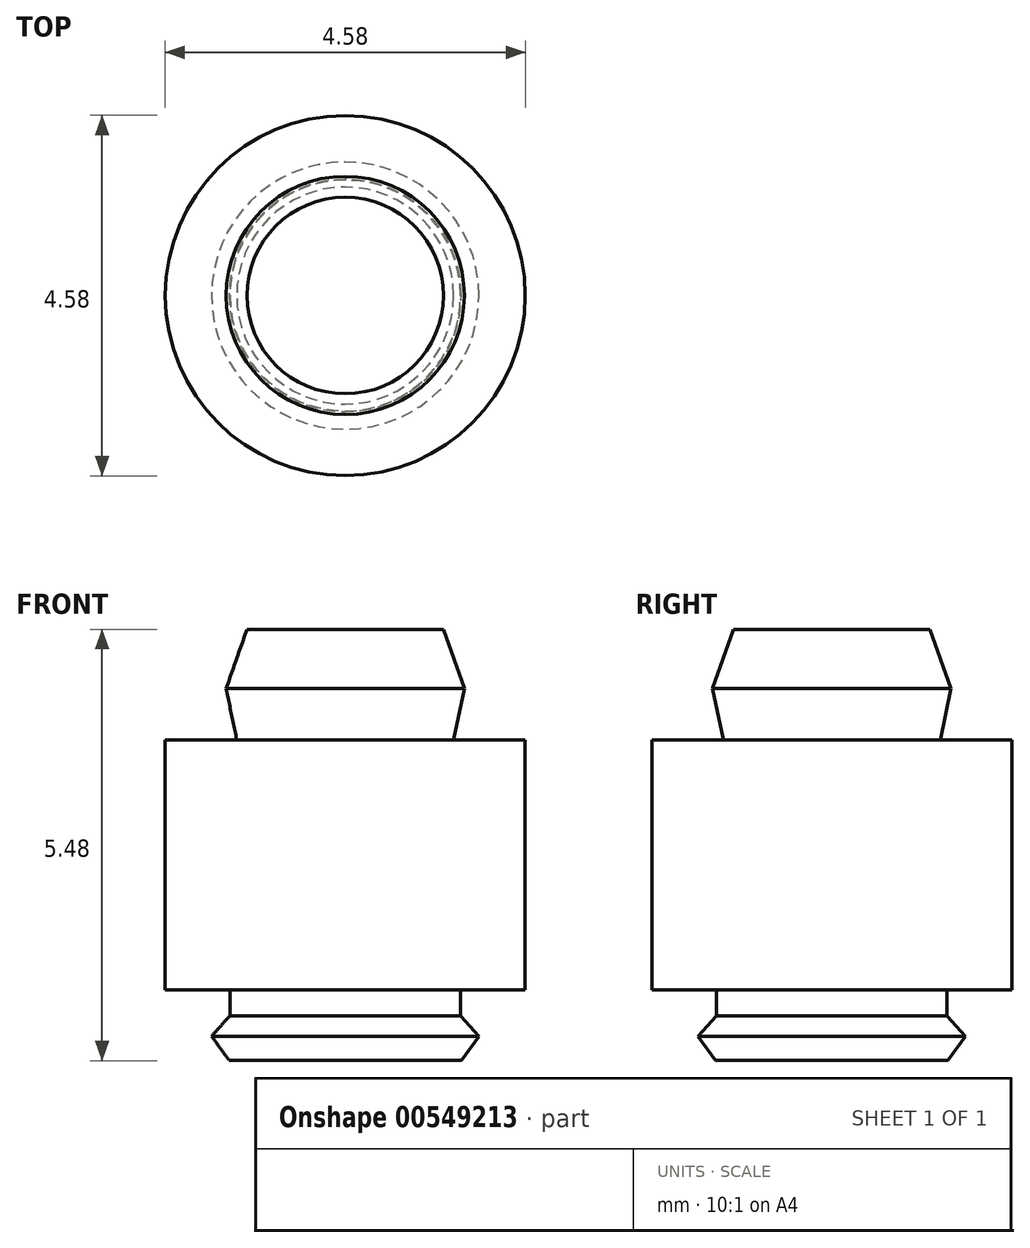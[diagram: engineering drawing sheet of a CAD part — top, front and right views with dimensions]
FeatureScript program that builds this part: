
annotation { "Feature Type Name" : "Feature", "Feature Type Description" : "" }
export const myFeature = defineFeature(function(context is Context, id is Id, definition is map)
    precondition{}
    {
        {
            var Q0;
            Q0=qCreatedBy(makeId("Front.planeOp"),FACE);
            var sketch = newSketch(context, id + "F0", { "sketchPlane" : qUnion([Q0])});
            skLineSegment(sketch, "E0", {"start": v(0, 0) * mm, "end": v(0, 4.84) * mm});
            skLineSegment(sketch, "E1", {"start": v(0, 3.18) * mm, "end": v(2.29, 3.18) * mm});
            skLineSegment(sketch, "E2", {"start": v(2.29, 3.18) * mm, "end": v(2.29, 0) * mm});
            skLineSegment(sketch, "E3", {"start": v(2.29, 0) * mm, "end": v(0, 0) * mm});
            skLineSegment(sketch, "E4", {"start": v(1.38, 3.18) * mm, "end": v(1.51, 3.83) * mm});
            skLineSegment(sketch, "E5", {"start": v(1.51, 3.83) * mm, "end": v(1.25, 4.58) * mm});
            skLineSegment(sketch, "E6", {"start": v(1.25, 4.58) * mm, "end": v(0, 4.58) * mm});
            skLineSegment(sketch, "E7", {"start": v(1.47, 0) * mm, "end": v(1.47, -0.33) * mm});
            skLineSegment(sketch, "E8", {"start": v(1.47, -0.33) * mm, "end": v(1.7, -0.59) * mm});
            skLineSegment(sketch, "E9", {"start": v(1.7, -0.59) * mm, "end": v(1.47, -0.9) * mm});
            skLineSegment(sketch, "E10", {"start": v(1.47, -0.9) * mm, "end": v(0, -0.9) * mm});
            skLineSegment(sketch, "E11", {"start": v(0, -0.9) * mm, "end": v(0, 0) * mm});
            skSolve(sketch);
        }
        {
            var Q0;
            {var subQ0=sQuery(id+"F0.wireOp",EDGE,"E4");Q0=makeQuery(id+"F0.imprint","IMPRINT",FACE,{"disambiguationData":[TD([[makeQuery(id+"F0.imprint","IMPRINT",EDGE,{"derivedFrom":subQ0}),1.0]])]});}
            var Q1;
            {var subQ0=sQuery(id+"F0.wireOp",EDGE,"E7");Q1=makeQuery(id+"F0.imprint","IMPRINT",FACE,{"disambiguationData":[TD([[makeQuery(id+"F0.imprint","IMPRINT",EDGE,{"derivedFrom":subQ0}),-1.0]])]});}
            var Q2;
            {var subQ0=sQuery(id+"F0.wireOp",EDGE,"E2");Q2=makeQuery(id+"F0.imprint","IMPRINT",FACE,{"disambiguationData":[TD([[makeQuery(id+"F0.imprint","IMPRINT",EDGE,{"derivedFrom":subQ0}),-1.0]])]});}
            var Q3;
            Q3=sQuery(id+"F0.wireOp",EDGE,"E0");
            revolve(context, id + "F1", {"entities" : qUnion([Q0, Q1, Q2]), "axis" : qUnion([Q3]), "revolveType" : RevolveType.FULL});
        }
    });
